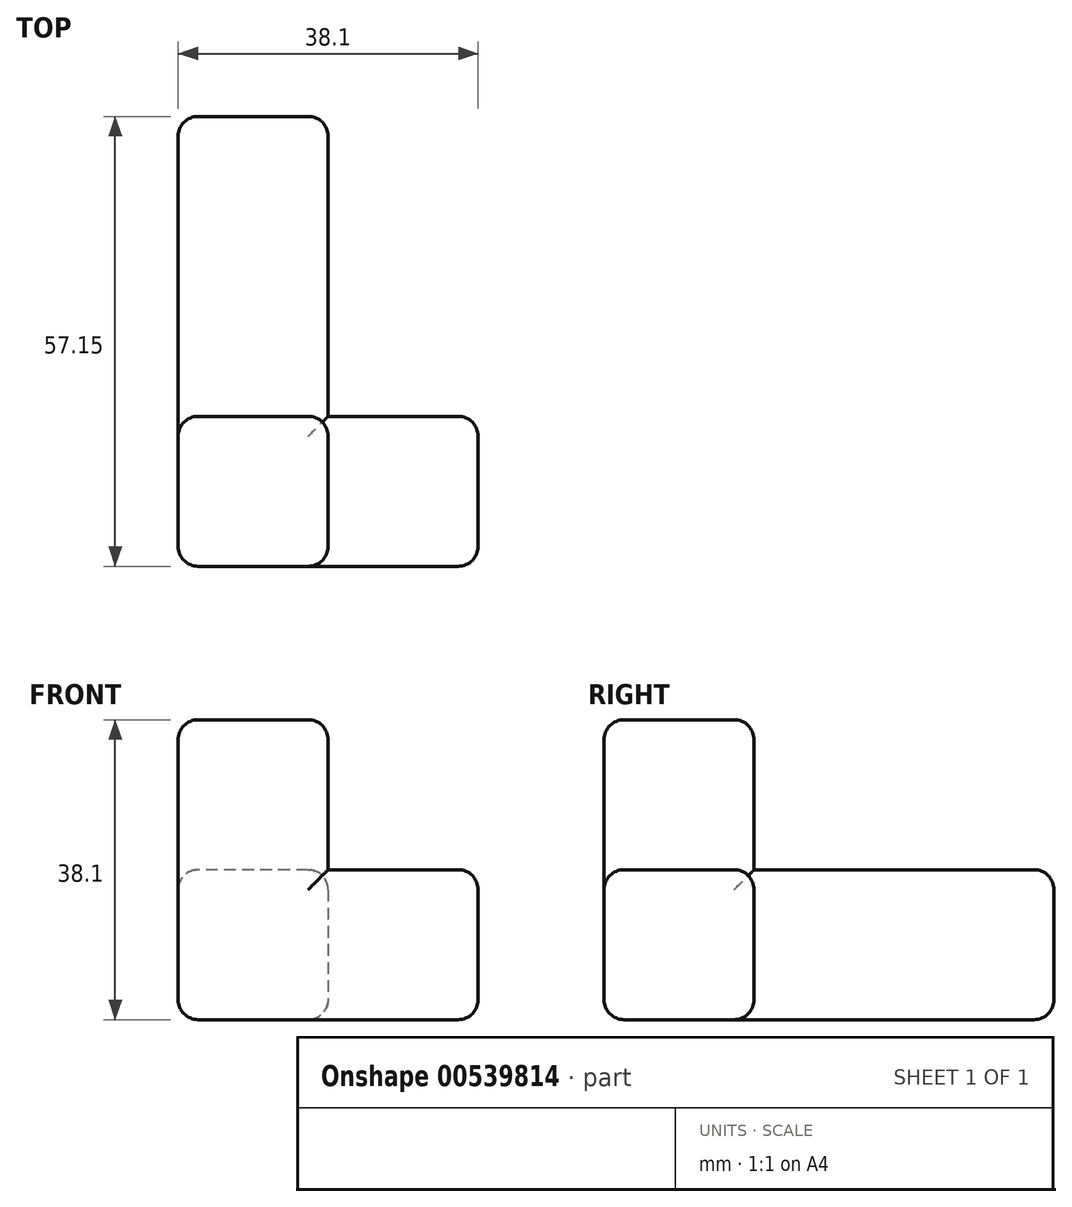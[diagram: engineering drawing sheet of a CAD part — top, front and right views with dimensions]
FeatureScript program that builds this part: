
annotation { "Feature Type Name" : "Feature", "Feature Type Description" : "" }
export const myFeature = defineFeature(function(context is Context, id is Id, definition is map)
    precondition{}
    {
        {
            var Q0;
            Q0=qCreatedBy(makeId("Top.planeOp"),FACE);
            var sketch = newSketch(context, id + "F0", { "sketchPlane" : qUnion([Q0])});
            skLineSegment(sketch, "E0", {"start": v(0, 0) * mm, "end": v(0, 57.15) * mm});
            skLineSegment(sketch, "E1", {"start": v(0, 57.15) * mm, "end": v(19.05, 57.15) * mm});
            skLineSegment(sketch, "E2", {"start": v(19.05, 57.15) * mm, "end": v(19.05, 19.05) * mm});
            skLineSegment(sketch, "E3", {"start": v(19.05, 19.05) * mm, "end": v(38.1, 19.05) * mm});
            skLineSegment(sketch, "E4", {"start": v(38.1, 19.05) * mm, "end": v(38.1, 0) * mm});
            skLineSegment(sketch, "E5", {"start": v(38.1, 0) * mm, "end": v(0, 0) * mm});
            skSolve(sketch);
        }
        {
            var Q0;
            Q0=makeQuery(id+"F0.imprint","IMPRINT",FACE,{"disambiguationData":[TD([[makeQuery(id+"F0.imprint","IMPRINT",EDGE,{"derivedFrom":sQuery(id+"F0.wireOp",EDGE,"E0")}),-1.0]])]});
            extrude(context, id + "F1", {"entities" : qUnion([Q0]), "depth" : 19.05 * mm, "offsetDistance" : 25.4 * mm});
        }
        {
            var Q0;
            Q0=makeQuery(id+"F1.opExtrude","CAP_FACE",FACE,{"disambiguationData":[OSD([sQuery(id+"F0.wireOp",EDGE,"E0"),sQuery(id+"F0.wireOp",EDGE,"E1"),sQuery(id+"F0.wireOp",EDGE,"E2"),sQuery(id+"F0.wireOp",EDGE,"E3"),sQuery(id+"F0.wireOp",EDGE,"E4"),sQuery(id+"F0.wireOp",EDGE,"E5")])],"isStart":false});
            var sketch = newSketch(context, id + "F2", { "sketchPlane" : qUnion([Q0])});
            skLineSegment(sketch, "E6.bottom", {"start": v(19.05, 19.05) * mm, "end": v(0, 19.05) * mm});
            skLineSegment(sketch, "E6.top", {"start": v(19.05, 0) * mm, "end": v(0, 0) * mm});
            skLineSegment(sketch, "E6.left", {"start": v(19.05, 19.05) * mm, "end": v(19.05, 0) * mm});
            skLineSegment(sketch, "E6.right", {"start": v(0, 19.05) * mm, "end": v(0, 0) * mm});
            skSolve(sketch);
        }
        {
            var Q0;
            Q0=makeQuery(id+"F2.imprint","IMPRINT",FACE,{"disambiguationData":[TD([[makeQuery(id+"F2.imprint","IMPRINT",EDGE,{"derivedFrom":sQuery(id+"F2.wireOp",EDGE,"E6.bottom")}),1.0]])]});
            extrude(context, id + "F3", {"entities" : qUnion([Q0]), "operationType" : NewBodyOperationType.ADD, "depth" : 19.05 * mm, "offsetDistance" : 25.4 * mm});
        }
        {
            var Q0;
            Q0=makeQuery(id+"F3.boolean.opBoolean","MERGE",FACE,{"derivedFrom":[makeQuery(id+"F1.opExtrude","SWEPT_FACE",FACE,{"disambiguationData":[OSD([sQuery(id+"F0.wireOp",EDGE,"E0")])]}),makeQuery(id+"F3.opExtrude","SWEPT_FACE",FACE,{"disambiguationData":[OSD([sQuery(id+"F2.wireOp",EDGE,"E6.right")])]})]});
            var Q1;
            Q1=makeQuery(id+"F3.opExtrude","CAP_FACE",FACE,{"disambiguationData":[OSD([sQuery(id+"F2.wireOp",EDGE,"E6.bottom"),sQuery(id+"F2.wireOp",EDGE,"E6.top"),sQuery(id+"F2.wireOp",EDGE,"E6.left"),sQuery(id+"F2.wireOp",EDGE,"E6.right")])],"isStart":false});
            var Q2;
            Q2=makeQuery(id+"F3.boolean.opBoolean","MERGE",FACE,{"derivedFrom":[makeQuery(id+"F1.opExtrude","SWEPT_FACE",FACE,{"disambiguationData":[OSD([sQuery(id+"F0.wireOp",EDGE,"E5")])]}),makeQuery(id+"F3.opExtrude","SWEPT_FACE",FACE,{"disambiguationData":[OSD([sQuery(id+"F2.wireOp",EDGE,"E6.top")])]})]});
            var Q3;
            Q3=makeQuery(id+"F1.opExtrude","CAP_FACE",FACE,{"disambiguationData":[OSD([sQuery(id+"F0.wireOp",EDGE,"E0"),sQuery(id+"F0.wireOp",EDGE,"E1"),sQuery(id+"F0.wireOp",EDGE,"E2"),sQuery(id+"F0.wireOp",EDGE,"E3"),sQuery(id+"F0.wireOp",EDGE,"E4"),sQuery(id+"F0.wireOp",EDGE,"E5")])],"isStart":true});
            var Q4;
            Q4=makeQuery(id+"F1.opExtrude","SWEPT_FACE",FACE,{"disambiguationData":[OSD([sQuery(id+"F0.wireOp",EDGE,"E1")])]});
            var Q5;
            Q5=makeQuery(id+"F1.opExtrude","SWEPT_FACE",FACE,{"disambiguationData":[OSD([sQuery(id+"F0.wireOp",EDGE,"E4")])]});
            var Q6;
            Q6=makeQuery(id+"F1.opExtrude","CAP_EDGE",EDGE,{"disambiguationData":[OSD([sQuery(id+"F0.wireOp",EDGE,"E2")])],"isStart":false});
            fillet(context, id + "F4", {"entities" : qUnion([Q0, Q1, Q2, Q3, Q4, Q5, Q6]), "radius" : 2.54 * mm, "tangentPropagation" : true, "allowEdgeOverflow" : false});
        }
        {
            var Q0;
            Q0=makeQuery(id+"F3.opExtrude","SWEPT_EDGE",EDGE,{"disambiguationData":[OSD([sQuery(id+"F0.wireOp",EDGE,"E2"),sQuery(id+"F0.wireOp",EDGE,"E3"),sQuery(id+"F2.wireOp",EDGE,"E6.bottom"),sQuery(id+"F2.wireOp",EDGE,"E6.left")])]});
            fillet(context, id + "F5", {"entities" : qUnion([Q0]), "radius" : 2.54 * mm, "tangentPropagation" : true, "allowEdgeOverflow" : false});
        }
        {
            var Q0;
            Q0=makeQuery(id+"F1.opExtrude","CAP_EDGE",EDGE,{"disambiguationData":[OSD([sQuery(id+"F0.wireOp",EDGE,"E3")])],"isStart":false});
            fillet(context, id + "F6", {"entities" : qUnion([Q0]), "radius" : 2.54 * mm, "tangentPropagation" : true, "allowEdgeOverflow" : false});
        }
    });
